# Revit family: HVAC-Chilled_Beam-Dadanco-ACB30
name_source: partatom
category: Mechanical Equipment
revit_build: Autodesk Revit 2018 (Build: 20170223_1515(x64)
units: mm (PartAtom-declared; Revit-internal decimal feet)

## family parameters
Always vertical = Yes
Cut with Voids When Loaded = No
OmniClass Number = 23.75.70.17.31
OmniClass Title = Induction Units
Part Type = Normal
Room Calculation Point = No
Round Connector Dimension = Use Radius
Shared = No
Work Plane-Based = No

## types (7) — shared parameters
2 Pipe Coil Configuration = Yes
2 or 4 pipe = 2
4 Pipe Coil Configuration = No
Assembly Code = D3040100
CWF = 0 GPM
CWPD = 0.00 ftH2O
Cooling Primary Air Dry Bulb = 0 °F
Cooling Primary Air Wet Bulb = 0 °F
Cooling Room Dry Bulb = 0 °F
Cooling Supply Air Temperature = 0 °F
Description = Active Chilled Beam
Drain Pan = No
Front_Back_or_Top_Inlet_radius = 0' - 2"
Generic Black color = Metal-Dadanco-Steel-Galvanized Black Powder Coat Finish
Generic White = Generic White Paint
HWF = 0 GPM
HWPD = 0.00 ftH2O
Heating Primary Air Dry Bulb = 0 °F
Heating Room Dry Bulb = 0 °F
Heating Supply Air Temperature = 0 °F
Housing Material = Metal-Dadanco-Steel-Galvanized
Keynote = 23 37 00.A1
Latent Cooling = 0.0 Btu/h
Manufacturer = Dadanco
Model = ACB30
Net Unit Cooling Sensible = 0.0 Btu/h
Net Unit Heating Sensible = 0.0 Btu/h
PA = 0 CFM
PASP = 0.00 in-wg
Primary Air Inlet Size = 0' - 4"
Revision Date = 03/24/2023
SCHW Temp Out = 0 °F
SCHW Temperature = 0 °F
SHHW Temp Out = 0 °F
SHHW Temperature = 0 °F
Secondary Air Sensible Cooling = 0.0 Btu/h
Secondary Air Sensible Heating = 0.0 Btu/h
Side Air Inlet Radius = 0' - 2"
Supply Air = 0 CFM
Total Cooling Capacity = 0.0 Btu/h
Type Comments = 1-way Discharge Vertical Coil
URL = http://www.dadanco.com
Unit Height = 1' - 5"
Unit Width = 0' - 7"
zero-valued in all types: Cooling Room Relative Humidity

## per-type parameters (varying)
| type | Drip Tray | Nominal Unit Length | Overall Unit Length | Pan | Unit Length | Unit Weight |
| 4' Nominal Length | No | 4' - 0" | 3' - 6" | No | 3' - 4" | 44 lb |
| 2' Nominal Length | No | 2' - 0" | 2' - 2" | No | 2' - 0" | 28 lb |
| 3' Nominal Length | No | 3' - 0" | 2' - 10" | No | 2' - 8" | 36 lb |
| 5' Nominal Length | No | 5' - 0" | 4' - 6" | No | 4' - 4" | 51 lb |
| 6' Nominal Length | Yes | 6' - 0" | 5' - 6" | Yes | 5' - 4" | 59 lb |
| 7' Nominal Length | No | 7' - 0" | 6' - 6" | No | 6' - 4" | 67 lb |
| 8' Nominal Length | No | 8' - 0" | 7' - 6" | No | 7' - 4" | 75 lb |

## geometry (parser evidence)
native form markers: Blend x30, Sweep x4
no freeform markers — native parametric forms only
